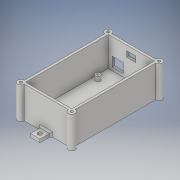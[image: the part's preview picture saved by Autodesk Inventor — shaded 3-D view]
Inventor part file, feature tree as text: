
AUTODESK INVENTOR PART (.ipt)
format: ipt  version: 2019 (Build 230136000, 136)  size: 450,048 bytes
history: native  units: mm
features: extrude x9, sketch x9, projected_geometry x4, mirror x3, chamfer x2
ambient origin geometry x8: Origin, YZ Plane, XZ Plane, XY Plane, X Axis, Y Axis, Z Axis, Center Point
bodies: Solid1 (feature_tree)
feature tree (27):
  extrude  "Extrusion1"  Depth=110.0mm
  extrude  "Extrusion2"  Depth=3.0mm
  extrude  "Extrusion3"  Depth=3.0mm
  extrude  "Extrusion4"  Depth=37.0mm TaperAngle=0.0deg
  extrude  "Extrusion5"  Depth=92.0mm
  extrude  "Extrusion6"  Depth=2.5mm
  extrude  "Extrusion7"  Depth=2.5mm
  mirror  "Mirror1"
  mirror  "Mirror2"
  extrude  "Extrusion9"  Depth=5.92mm
  chamfer  "Chamfer1"  Distance=6.0mm
  extrude  "Extrusion10"  Depth=6.0mm
  mirror  "Mirror3"
  chamfer  "Chamfer2"  Distance=6.0mm
  sketch  "Sketch1"  dims[d0=64.0mm d1=110.0mm]
  sketch  "Sketch2"  dims[d2=3.0mm d3=0.0mm d4=3.0mm]
  projected_geometry  "Projected Loop1"
  sketch  "Sketch3"  dims[d5=3.0mm d6=3.0mm]
  sketch  "Sketch4"  dims[d7=3.0mm d8=37.0mm d9=0.0mm]
  sketch  "Sketch5"  dims[d15=46.16mm d16=92.0mm]
  projected_geometry  "Projected Loop2"
  sketch  "Sketch7"  dims[d17=2.5mm d18=2.5mm]
  projected_geometry  "Projected Loop3"
  sketch  "Sketch8"  dims[d19=2.5mm d20=2.5mm]
  sketch  "Sketch10"  dims[d21=79.0mm d22=5.92mm]
  sketch  "Sketch11"  dims[d23=5.92mm d24=6.0mm d25=6.0mm d26=6.0mm d27=6.0mm d28=6.0mm d29=6.0mm d30=6.0mm d31=0.0mm d33=2.0mm d34=12.0mm d35=14.0mm d36=6.0mm d37=0.0mm d38=18.0mm d39=7.0mm d40=11.5mm d41=23.25mm d42=23.25mm d43=6.0mm d44=0.0mm d45=40.0mm d46=0.0mm d47=3.3mm d48=20.0mm d49=0.0mm d56=4.0mm d57=12.0mm d58=21.757359mm d59=21.757359mm d60=14.0mm d61=0.0mm d62=2.0mm d63=2.0mm d64=45.0deg d65=5.2mm d66=6.0mm d67=6.0mm d68=12.0mm d69=0.0mm d70=2.0mm d71=2.0mm d72=45.0deg d73=5.0mm]
  projected_geometry  "Projected Loop4"
